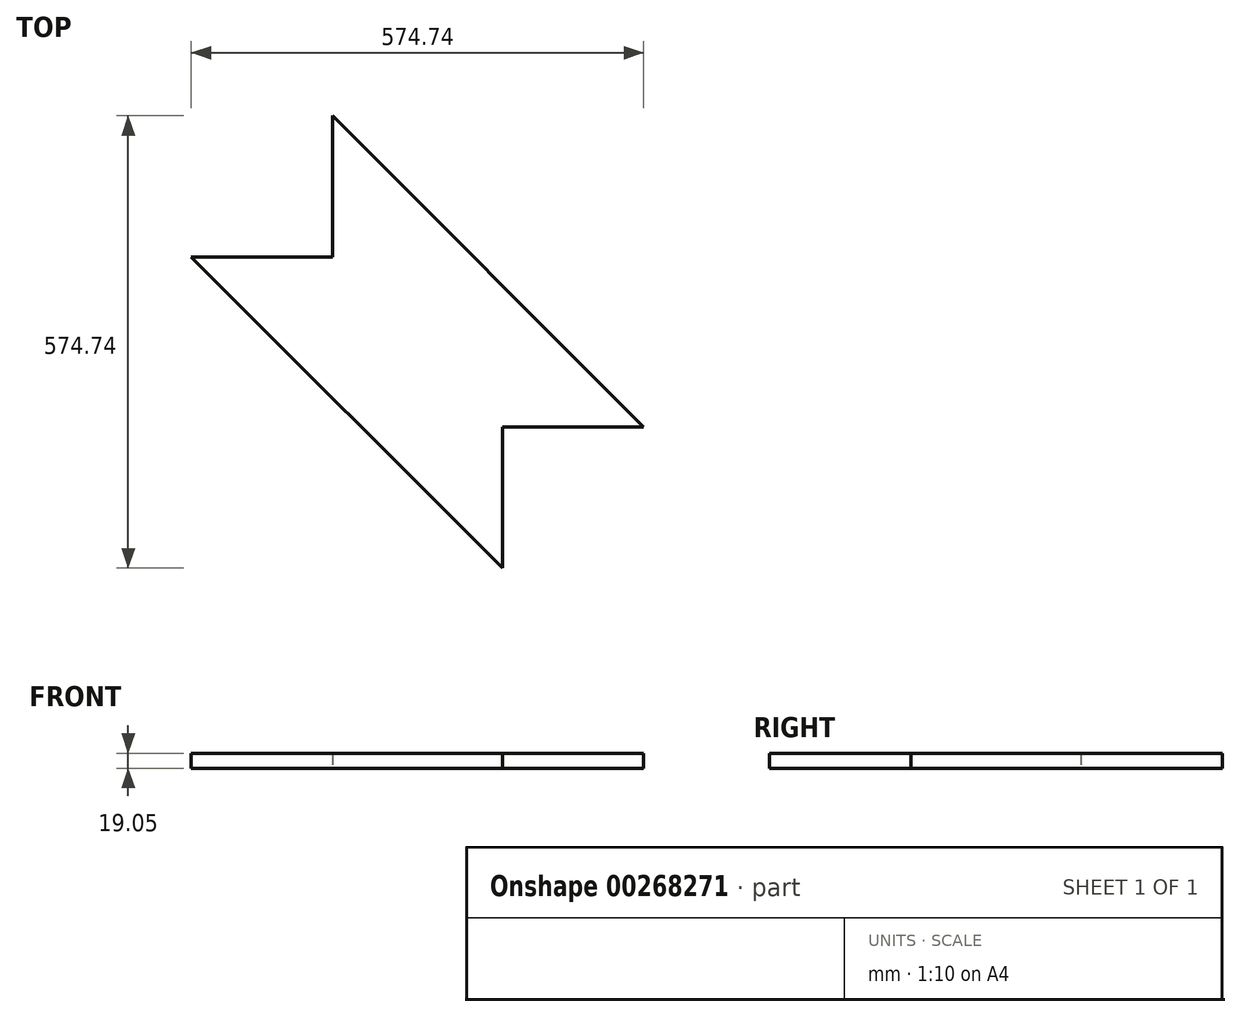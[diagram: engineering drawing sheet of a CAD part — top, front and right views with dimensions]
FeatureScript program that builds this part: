
annotation { "Feature Type Name" : "Feature", "Feature Type Description" : "" }
export const myFeature = defineFeature(function(context is Context, id is Id, definition is map)
    precondition{}
    {
        {
            var Q0;
            Q0=qCreatedBy(makeId("Top.planeOp"),FACE);
            var sketch = newSketch(context, id + "F0", { "sketchPlane" : qUnion([Q0])});
            skLineSegment(sketch, "E0.bottom", {"start": v(838.2, 1371.6) * mm, "end": v(-838.2, 1371.6) * mm});
            skLineSegment(sketch, "E0.top", {"start": v(838.2, -1371.6) * mm, "end": v(-838.2, -1371.6) * mm});
            skLineSegment(sketch, "E0.left", {"start": v(838.2, 1371.6) * mm, "end": v(838.2, -1371.6) * mm});
            skLineSegment(sketch, "E0.right", {"start": v(-838.2, 1371.6) * mm, "end": v(-838.2, -1371.6) * mm});
            skLineSegment(sketch, "E1", {"start": v(-287.37, 107.76) * mm, "end": v(107.76, -287.37) * mm});
            skLineSegment(sketch, "E2", {"start": v(107.76, -287.37) * mm, "end": v(287.37, -107.76) * mm, "construction": true});
            skLineSegment(sketch, "E3", {"start": v(287.37, -107.76) * mm, "end": v(-107.76, 287.37) * mm});
            skLineSegment(sketch, "E4", {"start": v(-107.76, 287.37) * mm, "end": v(-287.37, 107.76) * mm, "construction": true});
            skLineSegment(sketch, "E5", {"start": v(-107.76, 287.37) * mm, "end": v(107.76, -287.37) * mm, "construction": true});
            skLineSegment(sketch, "E6", {"start": v(287.37, -107.76) * mm, "end": v(-287.37, 107.76) * mm, "construction": true});
            skPoint(sketch, "E7", {"position": v(0, 0) * mm});
            skLineSegment(sketch, "E8", {"start": v(-287.37, 107.76) * mm, "end": v(-107.76, 107.76) * mm});
            skLineSegment(sketch, "E9", {"start": v(-107.76, 107.76) * mm, "end": v(-107.76, 287.37) * mm});
            skLineSegment(sketch, "E10", {"start": v(107.76, -287.37) * mm, "end": v(107.76, -107.76) * mm});
            skLineSegment(sketch, "E11", {"start": v(107.76, -107.76) * mm, "end": v(287.37, -107.76) * mm});
            skLineSegment(sketch, "E12", {"start": v(-107.76, 107.76) * mm, "end": v(107.76, -107.76) * mm});
            skSolve(sketch);
        }
        {
            var Q0;
            Q0=makeQuery(id+"F0.imprint","IMPRINT",FACE,{"disambiguationData":[TD([[makeQuery(id+"F0.imprint","IMPRINT",EDGE,{"derivedFrom":sQuery(id+"F0.wireOp",EDGE,"E1")}),1.0]])]});
            extrude(context, id + "F1", {"entities" : qUnion([Q0]), "depth" : 19.05 * mm});
        }
        {
            var Q0;
            Q0=makeQuery(id+"F0.imprint","IMPRINT",FACE,{"disambiguationData":[TD([[makeQuery(id+"F0.imprint","IMPRINT",EDGE,{"derivedFrom":sQuery(id+"F0.wireOp",EDGE,"E3")}),1.0]])]});
            extrude(context, id + "F2", {"entities" : qUnion([Q0]), "operationType" : NewBodyOperationType.ADD, "depth" : 19.05 * mm});
        }
    });
